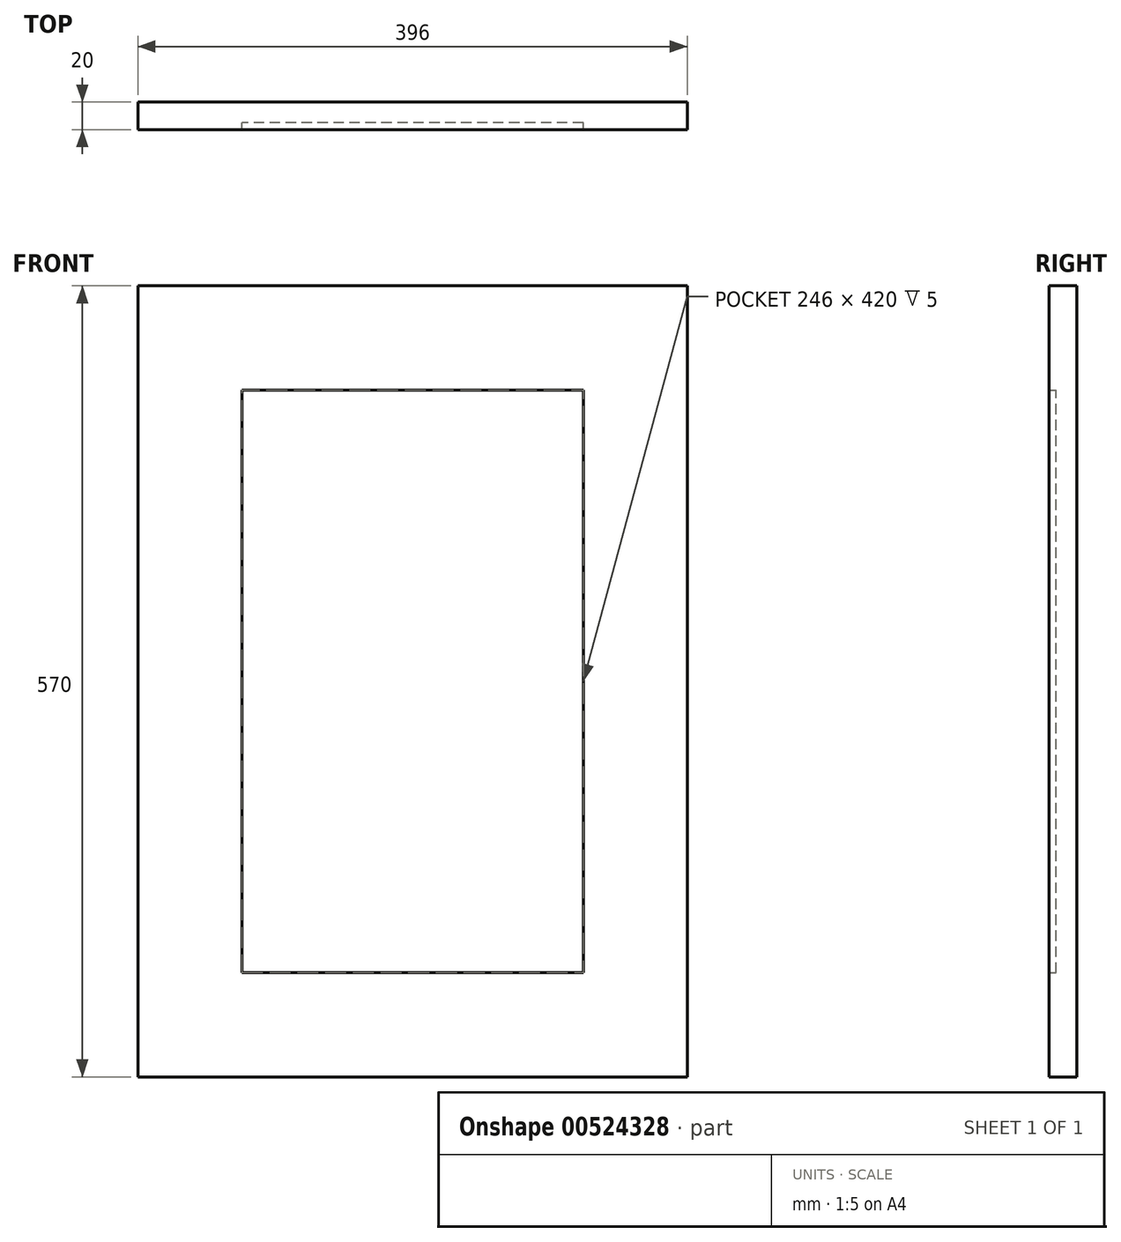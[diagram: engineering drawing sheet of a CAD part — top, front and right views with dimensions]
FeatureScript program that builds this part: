
annotation { "Feature Type Name" : "Feature", "Feature Type Description" : "" }
export const myFeature = defineFeature(function(context is Context, id is Id, definition is map)
    precondition{}
    {
        {
            var Q0;
            Q0=qCreatedBy(makeId("Front.planeOp"),FACE);
            var sketch = newSketch(context, id + "F0", { "sketchPlane" : qUnion([Q0])});
            skLineSegment(sketch, "E0.bottom", {"start": v(198, -285) * mm, "end": v(-198, -285) * mm});
            skLineSegment(sketch, "E0.top", {"start": v(198, 285) * mm, "end": v(-198, 285) * mm});
            skLineSegment(sketch, "E0.left", {"start": v(198, -285) * mm, "end": v(198, 285) * mm});
            skLineSegment(sketch, "E0.right", {"start": v(-198, -285) * mm, "end": v(-198, 285) * mm});
            skPoint(sketch, "E0.middle", {"position": v(0, 0) * mm});
            skLineSegment(sketch, "E1.0", {"start": v(123, 210) * mm, "end": v(-123, 210) * mm});
            skLineSegment(sketch, "E1.1", {"start": v(123, -210) * mm, "end": v(123, 210) * mm});
            skLineSegment(sketch, "E1.2", {"start": v(123, -210) * mm, "end": v(-123, -210) * mm});
            skLineSegment(sketch, "E1.3", {"start": v(-123, -210) * mm, "end": v(-123, 210) * mm});
            skSolve(sketch);
        }
        {
            var Q0;
            Q0=makeQuery(id+"F0.imprint","IMPRINT",FACE,{"disambiguationData":[TD([[makeQuery(id+"F0.imprint","IMPRINT",EDGE,{"derivedFrom":sQuery(id+"F0.wireOp",EDGE,"E1.0")}),1.0]])]});
            extrude(context, id + "F1", {"entities" : qUnion([Q0]), "depth" : 15 * mm, "offsetDistance" : 25 * mm});
        }
        {
            var Q0;
            Q0=makeQuery(id+"F0.imprint","IMPRINT",FACE,{"disambiguationData":[TD([[makeQuery(id+"F0.imprint","IMPRINT",EDGE,{"derivedFrom":sQuery(id+"F0.wireOp",EDGE,"E0.bottom")}),-1.0]])]});
            extrude(context, id + "F2", {"entities" : qUnion([Q0]), "operationType" : NewBodyOperationType.ADD, "depth" : 20 * mm, "offsetDistance" : 25 * mm});
        }
    });
